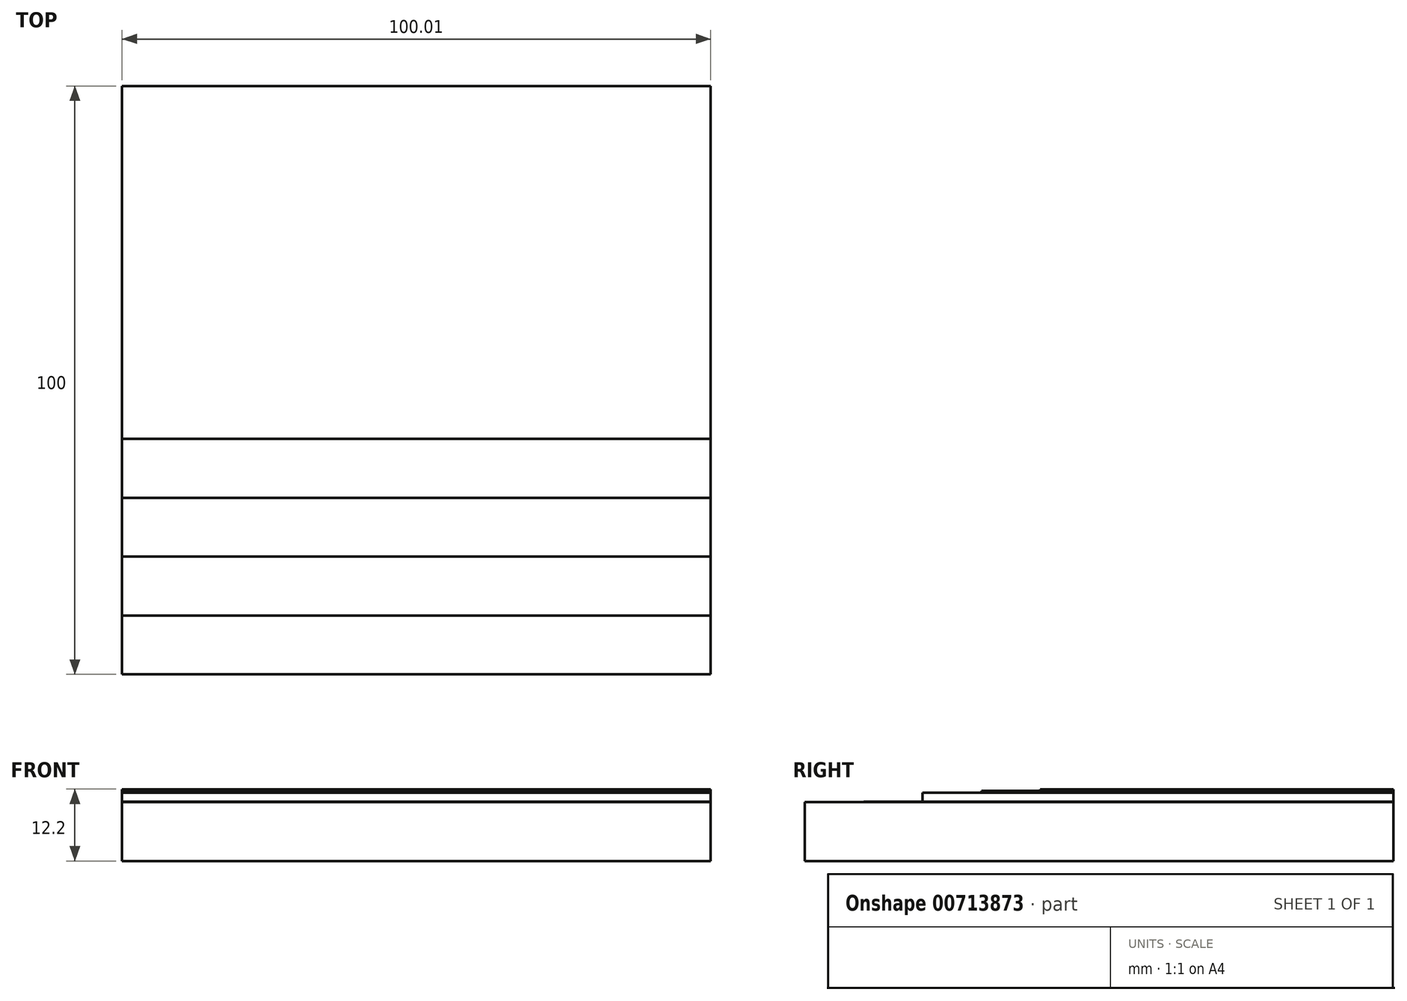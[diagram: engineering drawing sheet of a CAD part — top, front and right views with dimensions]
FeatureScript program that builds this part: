
annotation { "Feature Type Name" : "Feature", "Feature Type Description" : "" }
export const myFeature = defineFeature(function(context is Context, id is Id, definition is map)
    precondition{}
    {
        {
            var Q0;
            Q0=qCreatedBy(makeId("Front.planeOp"),FACE);
            var sketch = newSketch(context, id + "F0", { "sketchPlane" : qUnion([Q0])});
            skLineSegment(sketch, "E0.bottom", {"start": v(-75.12, -10.66) * mm, "end": v(24.88, -10.66) * mm});
            skLineSegment(sketch, "E0.top", {"start": v(-75.12, -20.66) * mm, "end": v(24.88, -20.66) * mm});
            skLineSegment(sketch, "E0.left", {"start": v(-75.12, -10.66) * mm, "end": v(-75.12, -20.66) * mm});
            skLineSegment(sketch, "E0.right", {"start": v(24.88, -10.66) * mm, "end": v(24.88, -20.66) * mm});
            skLineSegment(sketch, "E1", {"start": v(-75.12, -10.66) * mm, "end": v(-75.12, -10.56) * mm});
            skLineSegment(sketch, "E2", {"start": v(-75.12, -10.56) * mm, "end": v(24.89, -10.56) * mm});
            skLineSegment(sketch, "E3", {"start": v(24.89, -10.56) * mm, "end": v(24.88, -10.66) * mm});
            skLineSegment(sketch, "E4", {"start": v(-75.12, -10.56) * mm, "end": v(-75.12, -9.06) * mm});
            skLineSegment(sketch, "E5", {"start": v(-75.12, -9.06) * mm, "end": v(24.89, -9.06) * mm});
            skLineSegment(sketch, "E6", {"start": v(24.89, -9.06) * mm, "end": v(24.89, -10.56) * mm});
            skLineSegment(sketch, "E7", {"start": v(-75.12, -9.06) * mm, "end": v(-75.12, -8.76) * mm});
            skLineSegment(sketch, "E8", {"start": v(-75.12, -8.76) * mm, "end": v(24.89, -8.76) * mm});
            skLineSegment(sketch, "E9", {"start": v(24.89, -8.76) * mm, "end": v(24.89, -9.06) * mm});
            skLineSegment(sketch, "E10", {"start": v(-75.12, -8.76) * mm, "end": v(-75.12, -8.46) * mm});
            skLineSegment(sketch, "E11", {"start": v(-75.12, -8.46) * mm, "end": v(24.89, -8.46) * mm});
            skLineSegment(sketch, "E12", {"start": v(24.89, -8.46) * mm, "end": v(24.89, -8.76) * mm});
            skSolve(sketch);
        }
        {
            var Q0;
            Q0=makeQuery(id+"F0.imprint","IMPRINT",FACE,{"disambiguationData":[TD([[makeQuery(id+"F0.imprint","IMPRINT",EDGE,{"derivedFrom":sQuery(id+"F0.wireOp",EDGE,"E0.bottom")}),-1.0]])]});
            extrude(context, id + "F1", {"entities" : qUnion([Q0]), "depth" : 100 * mm});
        }
        {
            var Q0;
            Q0=makeQuery(id+"F0.imprint","IMPRINT",FACE,{"disambiguationData":[TD([[makeQuery(id+"F0.imprint","IMPRINT",EDGE,{"derivedFrom":sQuery(id+"F0.wireOp",EDGE,"E0.bottom")}),1.0]])]});
            extrude(context, id + "F2", {"entities" : qUnion([Q0]), "depth" : 90 * mm});
        }
        {
            var Q0;
            Q0=makeQuery(id+"F0.imprint","IMPRINT",FACE,{"disambiguationData":[TD([[makeQuery(id+"F0.imprint","IMPRINT",EDGE,{"derivedFrom":sQuery(id+"F0.wireOp",EDGE,"E2")}),1.0]])]});
            extrude(context, id + "F3", {"entities" : qUnion([Q0]), "depth" : 80 * mm});
        }
        {
            var Q0;
            Q0=makeQuery(id+"F0.imprint","IMPRINT",FACE,{"disambiguationData":[TD([[makeQuery(id+"F0.imprint","IMPRINT",EDGE,{"derivedFrom":sQuery(id+"F0.wireOp",EDGE,"E5")}),1.0]])]});
            extrude(context, id + "F4", {"entities" : qUnion([Q0]), "depth" : 70 * mm});
        }
        {
            var Q0;
            Q0=makeQuery(id+"F0.imprint","IMPRINT",FACE,{"disambiguationData":[TD([[makeQuery(id+"F0.imprint","IMPRINT",EDGE,{"derivedFrom":sQuery(id+"F0.wireOp",EDGE,"E8")}),1.0]])]});
            extrude(context, id + "F5", {"entities" : qUnion([Q0]), "depth" : 60 * mm});
        }
    });
